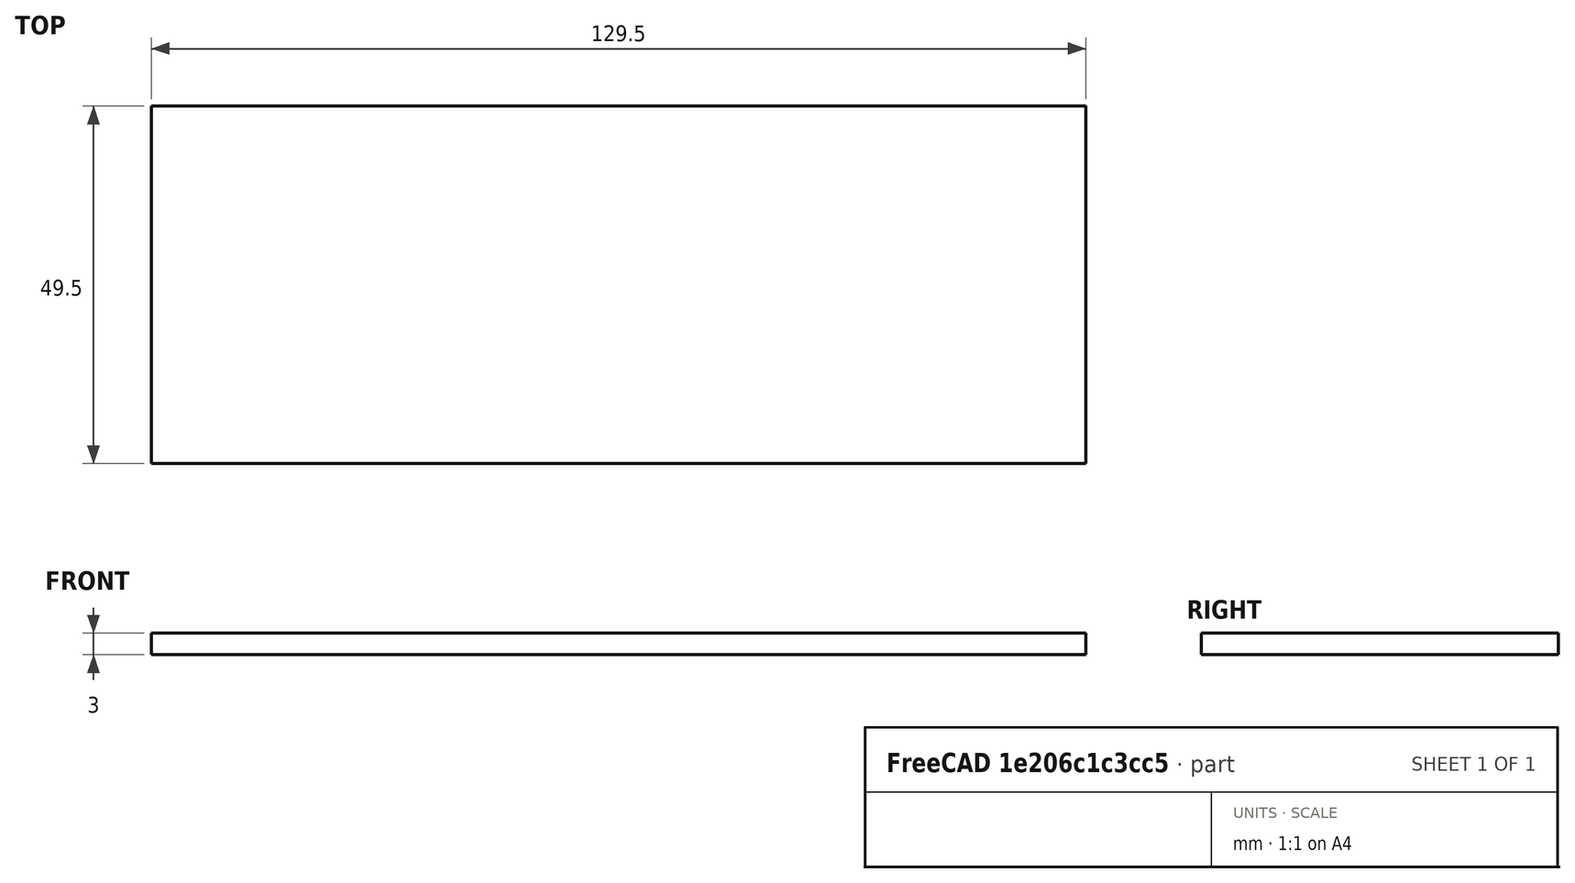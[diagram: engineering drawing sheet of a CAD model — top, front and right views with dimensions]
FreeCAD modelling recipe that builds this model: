
FCSTD DOCUMENT  (FreeCAD 0.16R6151 (Git))
Label: Sidepanel
License: All rights reserved
LicenseURL: http://en.wikipedia.org/wiki/All_rights_reserved
objects: Sketcher::SketchObject×1, PartDesign::Pad×1
note: 3 computed .brp shape members not serialized (recipe doc carries the construction recipe); baked Part::Feature solids carry a one-line shape summary decoded from their .brp

FEATURE [Sketcher::SketchObject] Sketch
  sketch-geometry (4):
    g0: LineSegment StartX=0 StartY=0 StartZ=0 EndX=129.5 EndY=0 EndZ=0
    g1: LineSegment StartX=129.5 StartY=0 StartZ=0 EndX=129.5 EndY=49.5 EndZ=0
    g2: LineSegment StartX=129.5 StartY=49.5 StartZ=0 EndX=0 EndY=49.5 EndZ=0
    g3: LineSegment StartX=0 StartY=49.5 StartZ=0 EndX=0 EndY=0 EndZ=0
  constraints (11):
    c: Coincident(g0,g1)
    c: Coincident(g1,g2)
    c: Coincident(g2,g3)
    c: Coincident(g3,g0)
    c: Horizontal(g0)
    c: Horizontal(g2)
    c: Vertical(g1)
    c: Vertical(g3)
    c: Coincident(g0,g-1)
    c: Distance(g1) = 49.5
    c: Distance(g2) = 129.5
FEATURE [PartDesign::Pad] Pad
  Length = 3
  Length2 = 100
  Sketch = -> Sketch
  Type = 0
